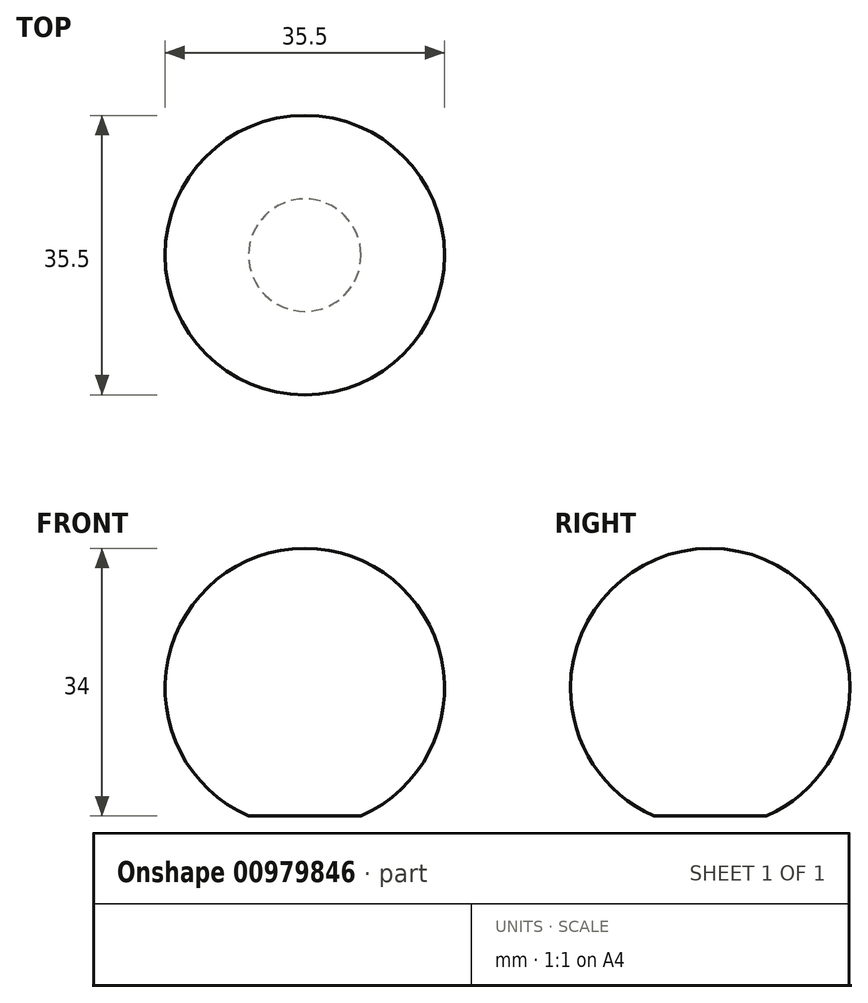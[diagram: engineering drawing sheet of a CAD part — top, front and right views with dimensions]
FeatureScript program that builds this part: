
annotation { "Feature Type Name" : "Feature", "Feature Type Description" : "" }
export const myFeature = defineFeature(function(context is Context, id is Id, definition is map)
    precondition{}
    {
        {
            var Q0;
            Q0=qCreatedBy(makeId("Top.planeOp"),FACE);
            var sketch = newSketch(context, id + "F0", { "sketchPlane" : qUnion([Q0])});
            skLineSegment(sketch, "E0.bottom", {"start": v(-17.75, 17.75) * mm, "end": v(17.75, 17.75) * mm});
            skLineSegment(sketch, "E0.top", {"start": v(-17.75, -17.75) * mm, "end": v(17.75, -17.75) * mm});
            skLineSegment(sketch, "E0.left", {"start": v(-17.75, 17.75) * mm, "end": v(-17.75, -17.75) * mm});
            skLineSegment(sketch, "E0.right", {"start": v(17.75, 17.75) * mm, "end": v(17.75, -17.75) * mm});
            skPoint(sketch, "E0.middle", {"position": v(0, 0) * mm});
            skSolve(sketch);
        }
        {
            var Q0;
            Q0=makeQuery(id+"F0.imprint","IMPRINT",FACE,{"disambiguationData":[TD([[makeQuery(id+"F0.imprint","IMPRINT",EDGE,{"derivedFrom":sQuery(id+"F0.wireOp",EDGE,"E0.bottom")}),-1.0]])]});
            extrude(context, id + "F1", {"entities" : qUnion([Q0]), "depth" : 35.5 * mm, "offsetDistance" : 25 * mm});
        }
        {
            var Q0;
            Q0=makeQuery(id+"F1.opExtrude","CAP_FACE",FACE,{"disambiguationData":[OSD([sQuery(id+"F0.wireOp",EDGE,"E0.bottom"),sQuery(id+"F0.wireOp",EDGE,"E0.top"),sQuery(id+"F0.wireOp",EDGE,"E0.left"),sQuery(id+"F0.wireOp",EDGE,"E0.right")])],"isStart":false});
            var Q1;
            Q1=makeQuery(id+"F1.opExtrude","SWEPT_FACE",FACE,{"disambiguationData":[OSD([sQuery(id+"F0.wireOp",EDGE,"E0.bottom")])]});
            var Q2;
            Q2=makeQuery(id+"F1.opExtrude","SWEPT_FACE",FACE,{"disambiguationData":[OSD([sQuery(id+"F0.wireOp",EDGE,"E0.right")])]});
            var Q3;
            Q3=makeQuery(id+"F1.opExtrude","CAP_FACE",FACE,{"disambiguationData":[OSD([sQuery(id+"F0.wireOp",EDGE,"E0.bottom"),sQuery(id+"F0.wireOp",EDGE,"E0.top"),sQuery(id+"F0.wireOp",EDGE,"E0.left"),sQuery(id+"F0.wireOp",EDGE,"E0.right")])],"isStart":true});
            var Q4;
            Q4=makeQuery(id+"F1.opExtrude","SWEPT_FACE",FACE,{"disambiguationData":[OSD([sQuery(id+"F0.wireOp",EDGE,"E0.left")])]});
            fillet(context, id + "F2", {"entities" : qUnion([Q0, Q1, Q2, Q3, Q4]), "radius" : 17.75 * mm, "tangentPropagation" : true, "allowEdgeOverflow" : false});
        }
        {
            var Q0;
            Q0=makeQuery(id+"F0.imprint","IMPRINT",FACE,{"disambiguationData":[TD([[makeQuery(id+"F0.imprint","IMPRINT",EDGE,{"derivedFrom":sQuery(id+"F0.wireOp",EDGE,"E0.bottom")}),-1.0]])]});
            extrude(context, id + "F3", {"entities" : qUnion([Q0]), "endBound" : BoundingType.SYMMETRIC, "depth" : 3 * mm, "offsetDistance" : 25 * mm});
        }
        {
            var Q0;
            Q0=makeQuery(id+"F3.opExtrude","SWEPT_BODY",BODY,{"disambiguationData":[OSD([sQuery(id+"F0.wireOp",EDGE,"E0.bottom"),sQuery(id+"F0.wireOp",EDGE,"E0.top"),sQuery(id+"F0.wireOp",EDGE,"E0.left"),sQuery(id+"F0.wireOp",EDGE,"E0.right")])]});
            var Q1;
            Q1=makeQuery(id+"F1.opExtrude","SWEPT_BODY",BODY,{"disambiguationData":[OSD([sQuery(id+"F0.wireOp",EDGE,"E0.bottom"),sQuery(id+"F0.wireOp",EDGE,"E0.top"),sQuery(id+"F0.wireOp",EDGE,"E0.left"),sQuery(id+"F0.wireOp",EDGE,"E0.right")])]});
            booleanBodies(context, id + "F4", {"operationType" : BooleanOperationType.SUBTRACTION, "tools" : qUnion([Q0]), "targets" : qUnion([Q1])});
        }
    });
